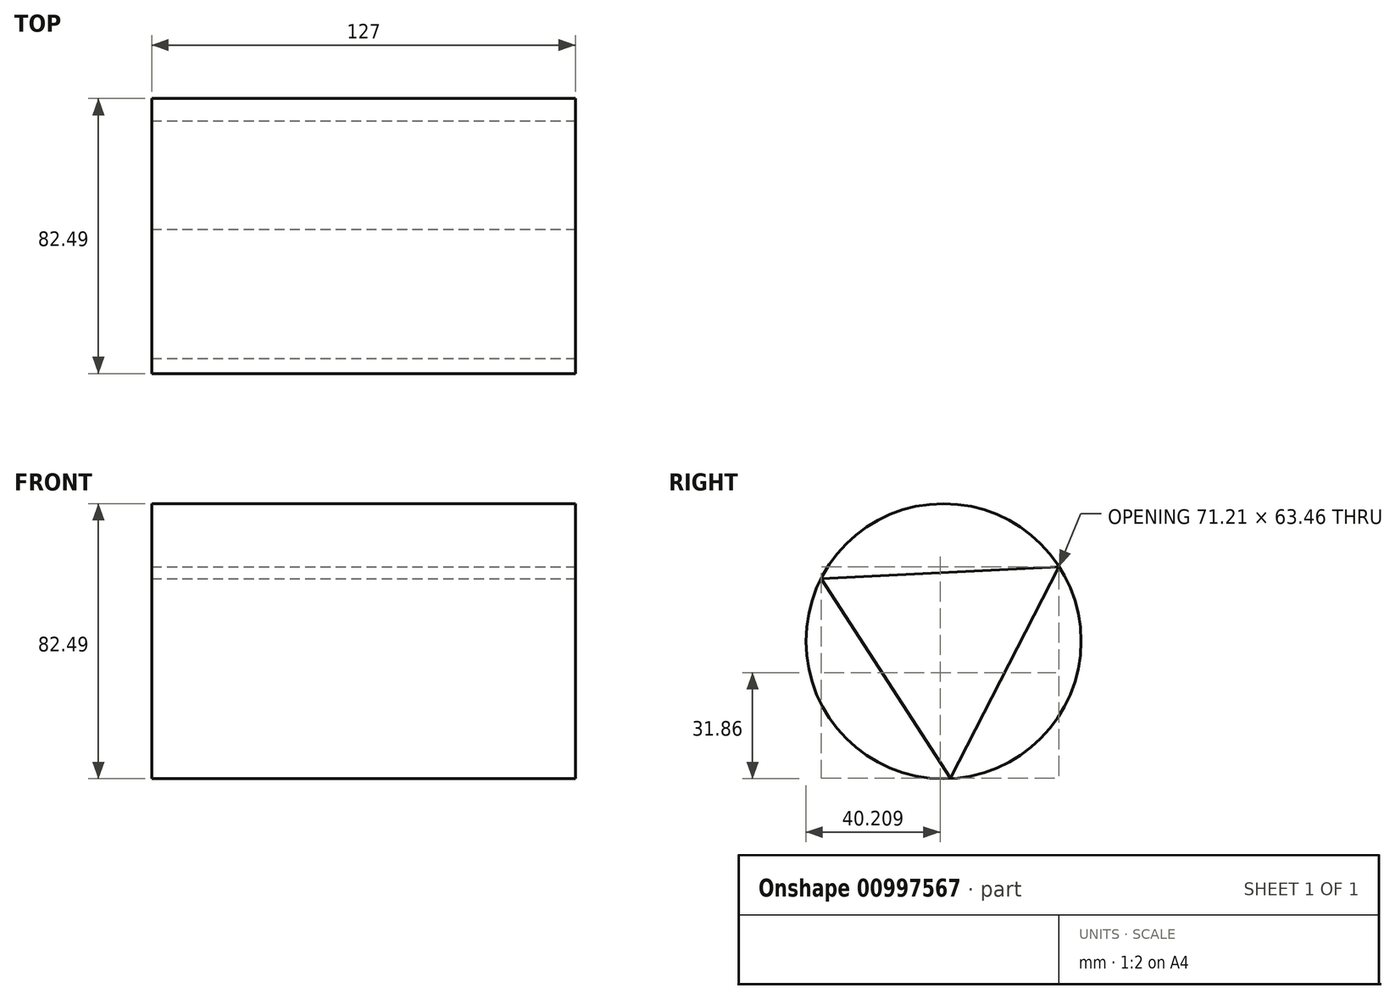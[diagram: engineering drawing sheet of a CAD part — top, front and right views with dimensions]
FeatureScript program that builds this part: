
annotation { "Feature Type Name" : "Feature", "Feature Type Description" : "" }
export const myFeature = defineFeature(function(context is Context, id is Id, definition is map)
    precondition{}
    {
        {
            var Q0;
            Q0=qCreatedBy(makeId("Right.planeOp"),FACE);
            var sketch = newSketch(context, id + "F0", { "sketchPlane" : qUnion([Q0])});
            skCircle(sketch, "E0", {"center": v(-18.32, 36.95) * mm, "radius": 41.24 * mm});
            skPoint(sketch, "E0.first.point", {"position": v(0, 0) * mm});
            skPoint(sketch, "E0.second.point", {"position": v(-37.49, 73.47) * mm});
            skPoint(sketch, "E0.third.point", {"position": v(-10.3, 77.41) * mm});
            skSolve(sketch);
        }
        {
            var Q0;
            Q0 = qSketchRegion(id + "F0", true);
            extrude(context, id + "F1", {"entities" : qUnion([Q0]), "depth" : 127 * mm, "offsetDistance" : 25.4 * mm});
        }
        {
            var Q0;
            Q0=makeQuery(id+"F1.opExtrude","CAP_FACE",FACE,{"disambiguationData":[OSD([sQuery(id+"F0.wireOp",EDGE,"E0")])],"isStart":false});
            var sketch = newSketch(context, id + "F2", { "sketchPlane" : qUnion([Q0])});
            skCircle(sketch, "E1.cCircle", {"center": v(-18.32, 36.95) * mm, "radius": 20.58 * mm, "construction": true});
            skLineSegment(sketch, "E1.0", {"start": v(16.25, 59.3) * mm, "end": v(-16.25, -4.16) * mm});
            skLineSegment(sketch, "E1.1", {"start": v(-16.25, -4.16) * mm, "end": v(-54.96, 55.72) * mm});
            skLineSegment(sketch, "E1.2", {"start": v(-54.96, 55.72) * mm, "end": v(16.25, 59.3) * mm});
            skPoint(sketch, "E1.0.midPoint", {"position": v(0, 27.57) * mm});
            skSolve(sketch);
        }
        {
            var Q0;
            Q0=makeQuery(id+"F2.imprint","IMPRINT",FACE,{"disambiguationData":[TD([[makeQuery(id+"F2.imprint","IMPRINT",EDGE,{"derivedFrom":sQuery(id+"F2.wireOp",EDGE,"E1.0")}),-1.0]])]});
            extrude(context, id + "F3", {"entities" : qUnion([Q0]), "operationType" : NewBodyOperationType.REMOVE, "oppositeDirection" : true, "depth" : 193.55 * mm, "offsetDistance" : 25.4 * mm});
        }
    });
